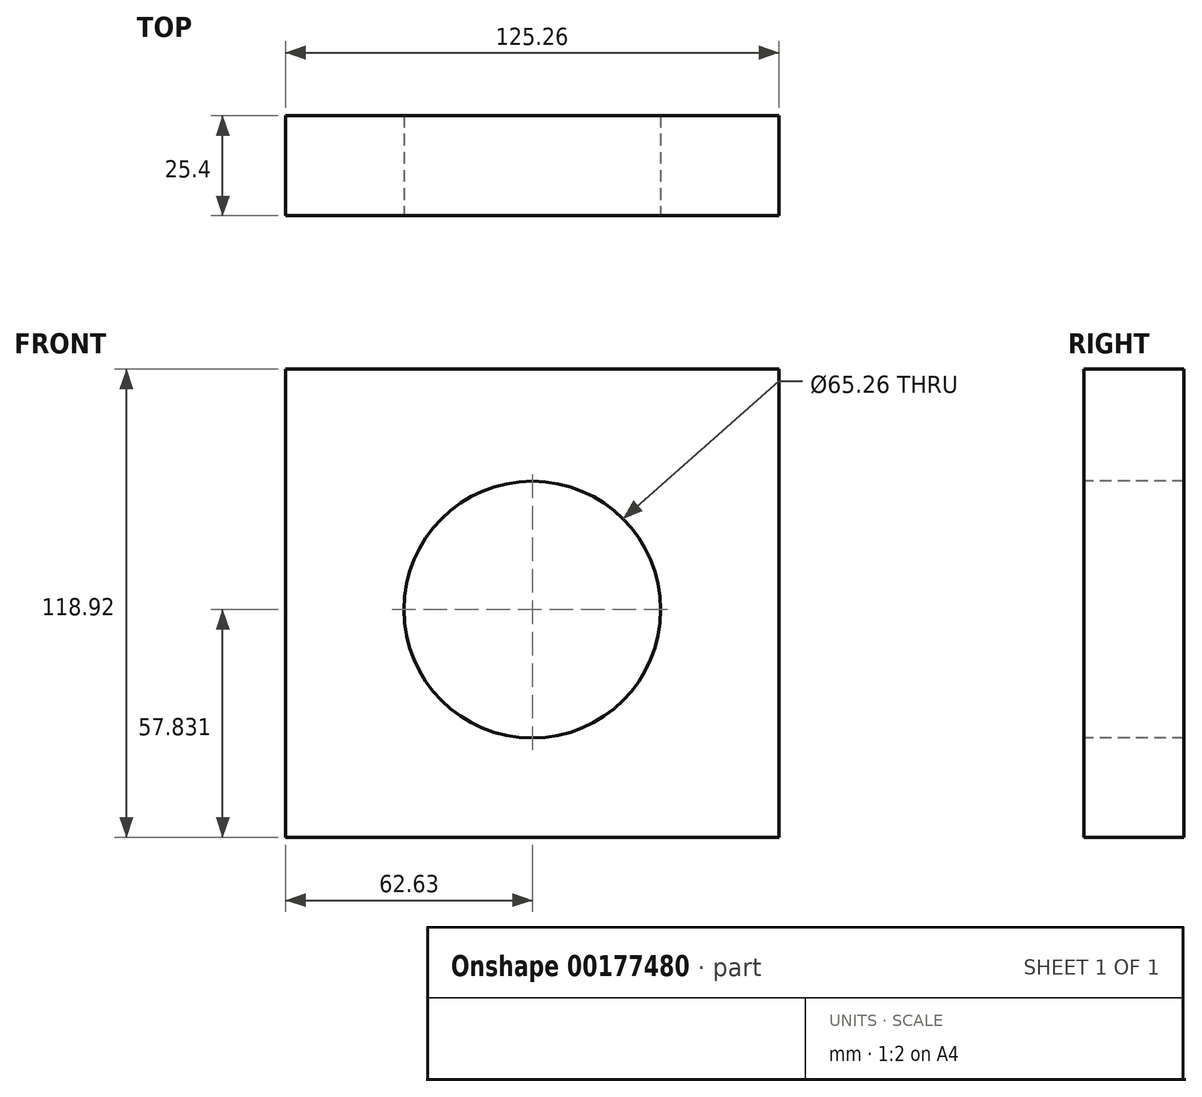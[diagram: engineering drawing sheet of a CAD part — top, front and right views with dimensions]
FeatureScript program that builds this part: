
annotation { "Feature Type Name" : "Feature", "Feature Type Description" : "" }
export const myFeature = defineFeature(function(context is Context, id is Id, definition is map)
    precondition{}
    {
        {
            var Q0;
            Q0=qCreatedBy(makeId("Front.planeOp"),FACE);
            var sketch = newSketch(context, id + "F0", { "sketchPlane" : qUnion([Q0])});
            skLineSegment(sketch, "E0.bottom", {"start": v(62.63, -59.46) * mm, "end": v(-62.63, -59.46) * mm});
            skLineSegment(sketch, "E0.top", {"start": v(62.63, 59.46) * mm, "end": v(-62.63, 59.46) * mm});
            skLineSegment(sketch, "E0.left", {"start": v(62.63, -59.46) * mm, "end": v(62.63, 59.46) * mm});
            skLineSegment(sketch, "E0.right", {"start": v(-62.63, -59.46) * mm, "end": v(-62.63, 59.46) * mm});
            skPoint(sketch, "E0.middle", {"position": v(0, 0) * mm});
            skCircle(sketch, "E1", {"center": v(0, -1.63) * mm, "radius": 32.63 * mm});
            skSolve(sketch);
        }
        {
            var Q0;
            Q0=makeQuery(id+"F0.imprint","IMPRINT",FACE,{"disambiguationData":[TD([[makeQuery(id+"F0.imprint","IMPRINT",EDGE,{"derivedFrom":sQuery(id+"F0.wireOp",EDGE,"E0.bottom")}),-1.0]])]});
            extrude(context, id + "F1", {"entities" : qUnion([Q0]), "oppositeDirection" : true, "depth" : 25.4 * mm});
        }
    });
